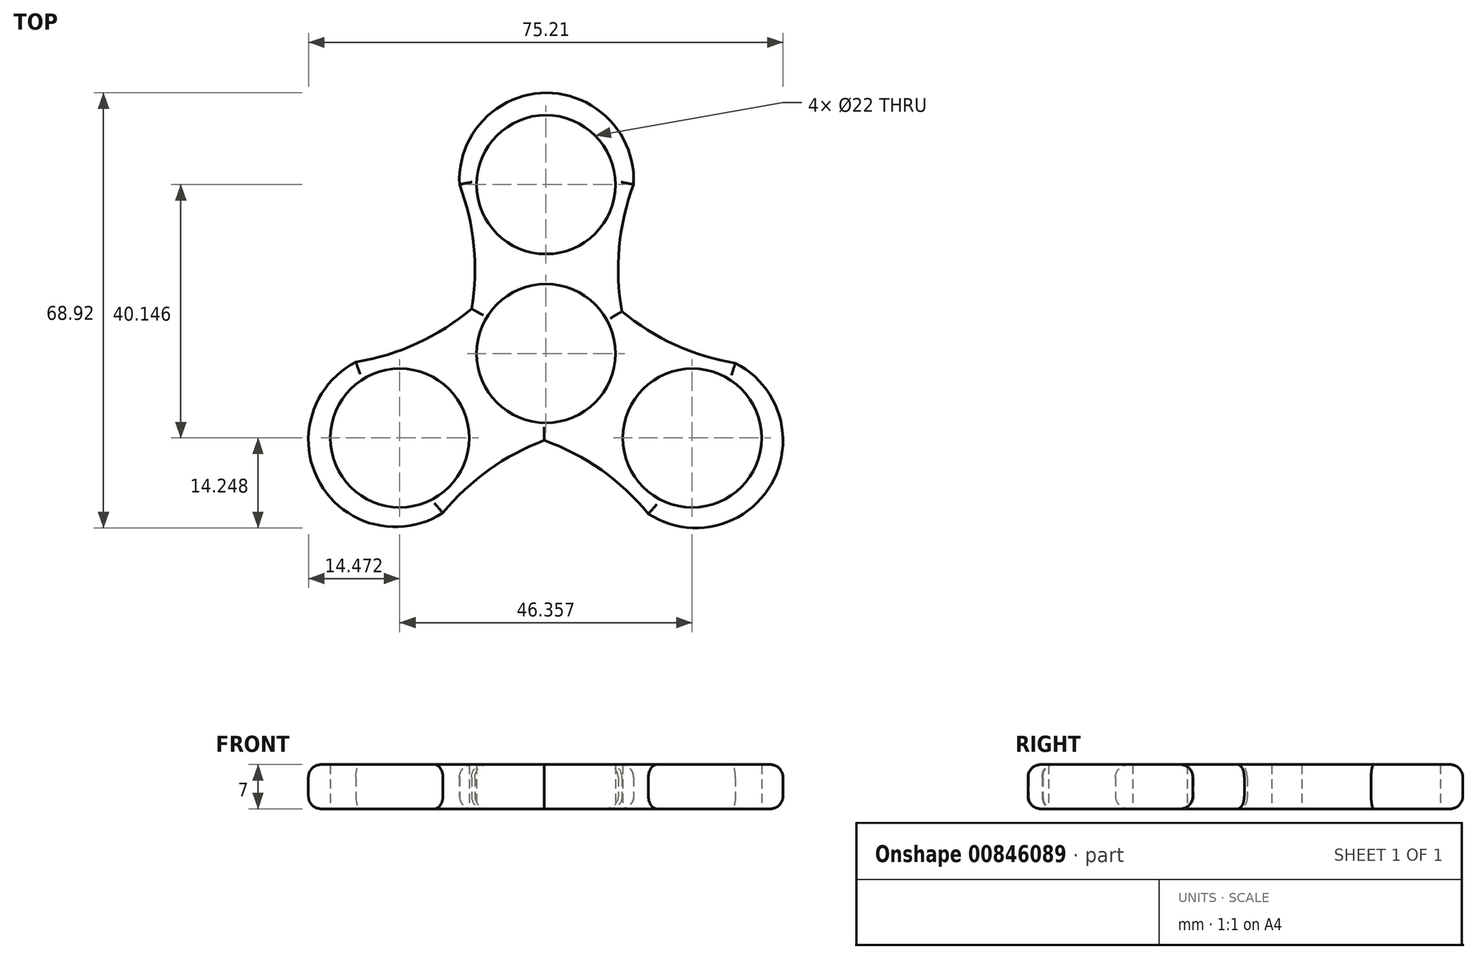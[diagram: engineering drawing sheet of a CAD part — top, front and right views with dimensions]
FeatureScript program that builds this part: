
annotation { "Feature Type Name" : "Feature", "Feature Type Description" : "" }
export const myFeature = defineFeature(function(context is Context, id is Id, definition is map)
    precondition{}
    {
        {
            var Q0;
            Q0=qCreatedBy(makeId("Top.planeOp"),FACE);
            var sketch = newSketch(context, id + "F0", { "sketchPlane" : qUnion([Q0])});
            skCircle(sketch, "E0", {"center": v(0, 0) * mm, "radius": 11 * mm});
            skCircle(sketch, "E1", {"center": v(0, 26.76) * mm, "radius": 11 * mm});
            skArc(sketch, "E2", {"start": v(13.88, 26.76) * mm, "mid": v(0.1, 41.3) * mm, "end": v(-13.7, 26.76) * mm});
            skArc(sketch, "E3", {"start": v(-11.79, 7.1) * mm, "mid": v(-11.44, 17.06) * mm, "end": v(-13.7, 26.76) * mm});
            skArc(sketch, "E4", {"start": v(13.88, 26.76) * mm, "mid": v(11.6, 16.83) * mm, "end": v(12.05, 6.66) * mm});
            skArc(sketch, "E5.1.0", {"start": v(-0.26, -13.76) * mm, "mid": v(-9.05, -18.44) * mm, "end": v(-16.33, -25.25) * mm});
            skArc(sketch, "E5.1.1", {"start": v(-30.12, -1.36) * mm, "mid": v(-35.8, -20.57) * mm, "end": v(-16.33, -25.25) * mm});
            skCircle(sketch, "E5.1.2", {"center": v(-23.18, -13.38) * mm, "radius": 11 * mm});
            skArc(sketch, "E5.1.3", {"start": v(-30.12, -1.36) * mm, "mid": v(-20.38, 1.63) * mm, "end": v(-11.79, 7.1) * mm});
            skArc(sketch, "E5.2.0", {"start": v(12.05, 6.66) * mm, "mid": v(20.5, 1.38) * mm, "end": v(30.03, -1.52) * mm});
            skArc(sketch, "E5.2.1", {"start": v(16.24, -25.4) * mm, "mid": v(35.71, -20.72) * mm, "end": v(30.03, -1.52) * mm});
            skCircle(sketch, "E5.2.2", {"center": v(23.18, -13.38) * mm, "radius": 11 * mm});
            skArc(sketch, "E5.2.3", {"start": v(16.24, -25.4) * mm, "mid": v(8.78, -18.47) * mm, "end": v(-0.26, -13.76) * mm});
            skPoint(sketch, "E6.orphan", {"position": v(-13.7, 0) * mm});
            skPoint(sketch, "E7.orphan", {"position": v(-6.94, 12.02) * mm});
            skPoint(sketch, "E8.orphan", {"position": v(6.85, 11.86) * mm});
            skPoint(sketch, "E9.orphan", {"position": v(13.88, 0) * mm});
            skPoint(sketch, "E10.orphan", {"position": v(6.85, -11.86) * mm});
            skPoint(sketch, "E11.orphan", {"position": v(-6.94, -12.02) * mm});
            skSolve(sketch);
        }
        {
            var Q0;
            Q0=qSketchRegion(id+"F0",true);
            extrude(context, id + "F1", {"entities" : qUnion([Q0]), "depth" : 7 * mm, "offsetDistance" : 25 * mm});
        }
        {
            var Q0;
            Q0=makeQuery(id+"F1.opExtrude","CAP_EDGE",EDGE,{"disambiguationData":[OSD([sQuery(id+"F0.wireOp",EDGE,"E3")])],"isStart":false});
            var Q1;
            Q1=makeQuery(id+"F1.opExtrude","CAP_EDGE",EDGE,{"disambiguationData":[OSD([sQuery(id+"F0.wireOp",EDGE,"E2")])],"isStart":false});
            var Q2;
            Q2=makeQuery(id+"F1.opExtrude","CAP_EDGE",EDGE,{"disambiguationData":[OSD([sQuery(id+"F0.wireOp",EDGE,"E4")])],"isStart":false});
            var Q3;
            Q3=makeQuery(id+"F1.opExtrude","CAP_EDGE",EDGE,{"disambiguationData":[OSD([sQuery(id+"F0.wireOp",EDGE,"E5.2.0")])],"isStart":false});
            var Q4;
            Q4=makeQuery(id+"F1.opExtrude","CAP_EDGE",EDGE,{"disambiguationData":[OSD([sQuery(id+"F0.wireOp",EDGE,"E5.2.1")])],"isStart":false});
            var Q5;
            Q5=makeQuery(id+"F1.opExtrude","CAP_EDGE",EDGE,{"disambiguationData":[OSD([sQuery(id+"F0.wireOp",EDGE,"E5.2.3")])],"isStart":false});
            var Q6;
            Q6=makeQuery(id+"F1.opExtrude","CAP_EDGE",EDGE,{"disambiguationData":[OSD([sQuery(id+"F0.wireOp",EDGE,"E5.1.0")])],"isStart":false});
            var Q7;
            Q7=makeQuery(id+"F1.opExtrude","CAP_EDGE",EDGE,{"disambiguationData":[OSD([sQuery(id+"F0.wireOp",EDGE,"E5.1.1")])],"isStart":false});
            var Q8;
            Q8=makeQuery(id+"F1.opExtrude","CAP_EDGE",EDGE,{"disambiguationData":[OSD([sQuery(id+"F0.wireOp",EDGE,"E5.1.3")])],"isStart":false});
            fillet(context, id + "F2", {"entities" : qUnion([Q0, Q1, Q2, Q3, Q4, Q5, Q6, Q7, Q8]), "radius" : 2 * mm, "tangentPropagation" : true, "allowEdgeOverflow" : false});
        }
        {
            var Q0;
            Q0=makeQuery(id+"F1.opExtrude","CAP_EDGE",EDGE,{"disambiguationData":[OSD([sQuery(id+"F0.wireOp",EDGE,"E2")])],"isStart":true});
            var Q1;
            Q1=makeQuery(id+"F1.opExtrude","CAP_EDGE",EDGE,{"disambiguationData":[OSD([sQuery(id+"F0.wireOp",EDGE,"E3")])],"isStart":true});
            var Q2;
            Q2=makeQuery(id+"F1.opExtrude","CAP_EDGE",EDGE,{"disambiguationData":[OSD([sQuery(id+"F0.wireOp",EDGE,"E5.1.3")])],"isStart":true});
            var Q3;
            Q3=makeQuery(id+"F1.opExtrude","CAP_EDGE",EDGE,{"disambiguationData":[OSD([sQuery(id+"F0.wireOp",EDGE,"E5.1.1")])],"isStart":true});
            var Q4;
            Q4=makeQuery(id+"F1.opExtrude","CAP_EDGE",EDGE,{"disambiguationData":[OSD([sQuery(id+"F0.wireOp",EDGE,"E5.1.0")])],"isStart":true});
            var Q5;
            Q5=makeQuery(id+"F1.opExtrude","CAP_EDGE",EDGE,{"disambiguationData":[OSD([sQuery(id+"F0.wireOp",EDGE,"E5.2.3")])],"isStart":true});
            var Q6;
            Q6=makeQuery(id+"F1.opExtrude","CAP_EDGE",EDGE,{"disambiguationData":[OSD([sQuery(id+"F0.wireOp",EDGE,"E5.2.1")])],"isStart":true});
            var Q7;
            Q7=makeQuery(id+"F1.opExtrude","CAP_EDGE",EDGE,{"disambiguationData":[OSD([sQuery(id+"F0.wireOp",EDGE,"E5.2.0")])],"isStart":true});
            var Q8;
            Q8=makeQuery(id+"F1.opExtrude","CAP_EDGE",EDGE,{"disambiguationData":[OSD([sQuery(id+"F0.wireOp",EDGE,"E4")])],"isStart":true});
            fillet(context, id + "F3", {"entities" : qUnion([Q0, Q1, Q2, Q3, Q4, Q5, Q6, Q7, Q8]), "radius" : 2 * mm, "tangentPropagation" : true, "allowEdgeOverflow" : false});
        }
    });
